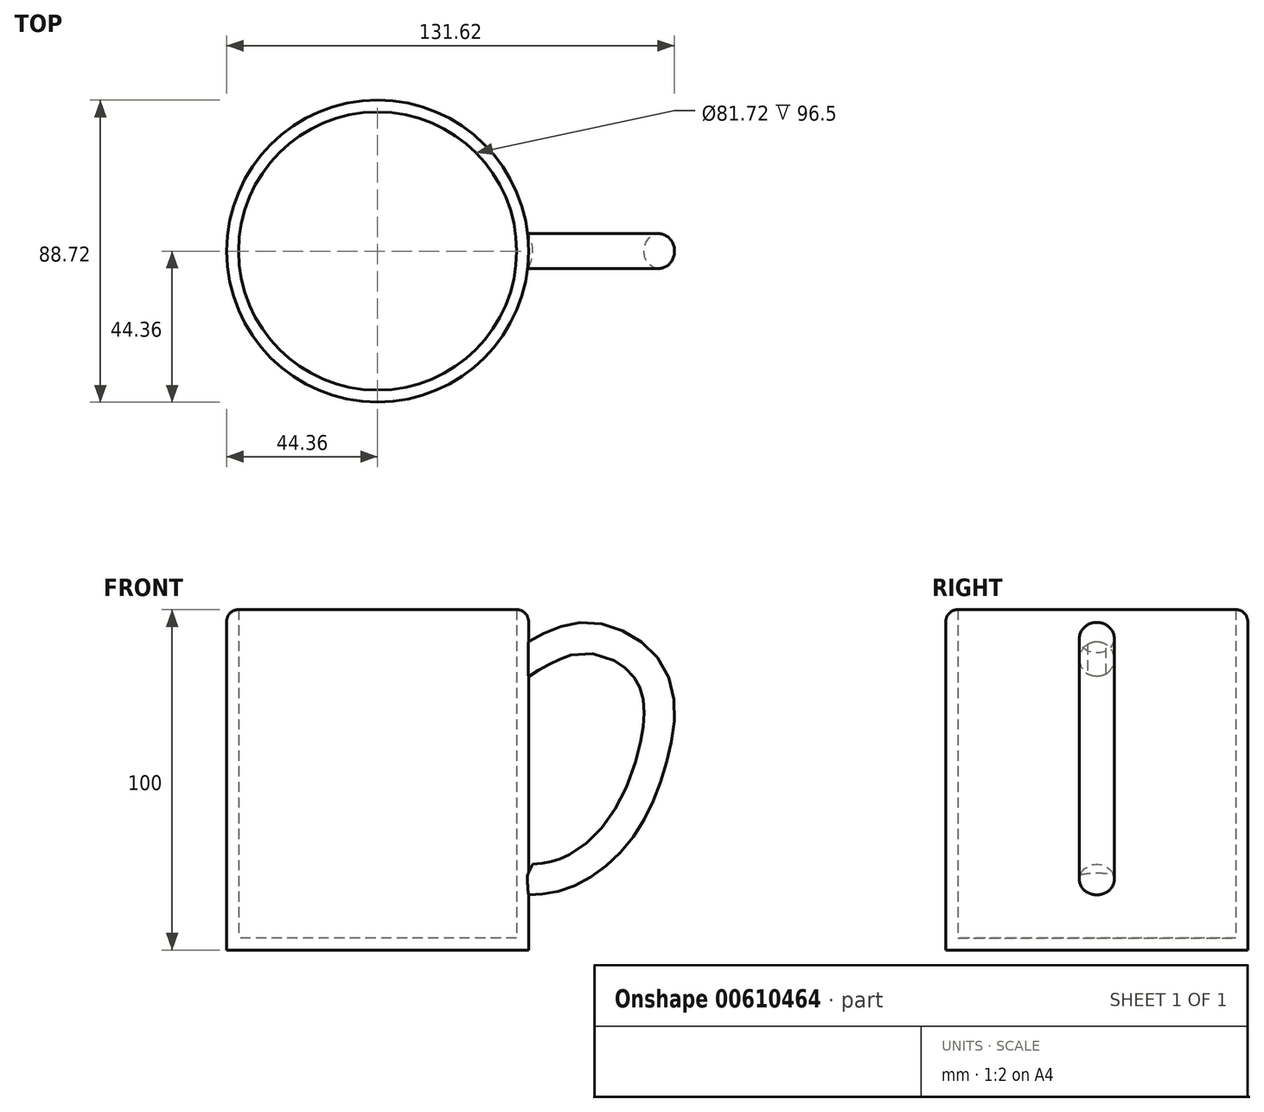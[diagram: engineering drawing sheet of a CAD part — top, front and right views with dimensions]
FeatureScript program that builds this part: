
annotation { "Feature Type Name" : "Feature", "Feature Type Description" : "" }
export const myFeature = defineFeature(function(context is Context, id is Id, definition is map)
    precondition{}
    {
        {
            var Q0;
            Q0=qCreatedBy(makeId("Top.planeOp"),FACE);
            var sketch = newSketch(context, id + "F0", { "sketchPlane" : qUnion([Q0])});
            skCircle(sketch, "E0", {"center": v(0, 0) * mm, "radius": 44.36 * mm});
            skSolve(sketch);
        }
        {
            var Q0;
            Q0 = qSketchRegion(id + "F0", true);
            extrude(context, id + "F1", {"entities" : qUnion([Q0]), "depth" : 100 * mm, "offsetDistance" : 25 * mm});
        }
        {
            var Q0;
            Q0=makeQuery(id+"F1.opExtrude","CAP_FACE",FACE,{"disambiguationData":[OSD([sQuery(id+"F0.wireOp",EDGE,"E0")])],"isStart":false});
            shell(context, id + "F2", {"entities" : qUnion([Q0]), "thickness" : 3.5 * mm});
        }
        {
            var Q0;
            Q0=makeQuery(id+"F1.opExtrude","CAP_EDGE",EDGE,{"disambiguationData":[OSD([sQuery(id+"F0.wireOp",EDGE,"E0")])],"isStart":false});
            fillet(context, id + "F3", {"entities" : qUnion([Q0]), "radius" : 3.5 * mm, "tangentPropagation" : true, "allowEdgeOverflow" : false});
        }
        {
            var Q0;
            Q0=qCreatedBy(makeId("Front.planeOp"),FACE);
            var sketch = newSketch(context, id + "F4", { "sketchPlane" : qUnion([Q0])});
            skFitSpline(sketch, "E1", {"points": [v(44.28, 83.34) * mm, v(61.73, 89.76) * mm, v(78.41, 80) * mm, v(79.18, 58.19) * mm, v(68.92, 35.6) * mm, v(54.8, 24.56) * mm, v(44.28, 22.51) * mm], "startDerivative": vector(100.83, 59.66) * mm, "endDerivative": vector(-81, -6.88) * mm});
            skSolve(sketch);
        }
        {
            var Q0;
            Q0=qCreatedBy(makeId("Right.planeOp"),FACE);
            cPlane(context, id + "F5", {"entities" : qUnion([Q0]), "cplaneType" : CPlaneType.OFFSET, "offset" : 44.36 * mm, "width" : 150 * mm, "height" : 150 * mm});
        }
        {
            var Q0;
            Q0=qCreatedBy(id+"F5.planeOp",FACE);
            var sketch = newSketch(context, id + "F6", { "sketchPlane" : qUnion([Q0])});
            skCircle(sketch, "E2", {"center": v(0, 85.51) * mm, "radius": 5.11 * mm});
            skSolve(sketch);
        }
        {
            var Q0;
            Q0=makeQuery(id+"F6.imprint","IMPRINT",FACE,{"disambiguationData":[TD([[makeQuery(id+"F6.imprint","IMPRINT",EDGE,{"derivedFrom":sQuery(id+"F6.wireOp",EDGE,"E2")}),1.0]])]});
            var Q1;
            Q1=sQuery(id+"F4.wireOp",EDGE,"E1");
            sweep(context, id + "F7", {"operationType" : NewBodyOperationType.ADD, "profiles" : qUnion([Q0]), "path" : qUnion([Q1])});
        }
    });
